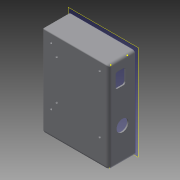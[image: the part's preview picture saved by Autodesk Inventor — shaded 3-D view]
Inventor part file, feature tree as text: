
AUTODESK INVENTOR PART (.ipt)
format: ipt  version: 2014 (Build 180170000, 170)  size: 323,584 bytes
history: native  units: mm
features: sketch x9, extrude x8, other x5, fillet x4, projected_geometry x1
ambient origin geometry x8: Origin, YZ Plane, XZ Plane, XY Plane, X Axis, Y Axis, Z Axis, Center Point
bodies: Body1 (feature_tree)
feature tree (27):
  other  "ソリッド1"
  extrude  "押し出し1"  TaperAngle=0.0deg  [1 undecoded]
  extrude  "押し出し2"  Depth=49.0mm
  extrude  "押し出し3"  TaperAngle=0.0deg  [1 undecoded]
  sketch  "スケッチ4"
  extrude  "押し出し4"  Depth=2.6mm
  extrude  "押し出し5"  Depth=2.6mm
  other  "作業平面1"
  extrude  "押し出し8"  Depth=2.6mm
  other  "面の勾配1"
  sketch  "スケッチ11"
  other  "面の勾配2"
  fillet  "フィレット4"  Radius=2.0mm
  fillet  "フィレット5"  Radius=1.4mm
  fillet  "フィレット6"  Radius=1.4mm
  extrude  "押し出し12"  Depth=1.4mm
  other  "面の勾配3"
  fillet  "フィレット8"  Radius=7.0mm
  extrude  "押し出し13"  Depth=58.0mm
  sketch  "スケッチ1"
  sketch  "スケッチ2"
  sketch  "スケッチ3"
  sketch  "スケッチ5"
  projected_geometry  "投影ループ1"
  sketch  "スケッチ9"
  sketch  "スケッチ15"
  sketch  "スケッチ16"
note: 2 required parameter values undecoded (feature->parameter linkage not recoverable at this tier; creation-order binding heuristic only, values carry confidence <= 0.55)
